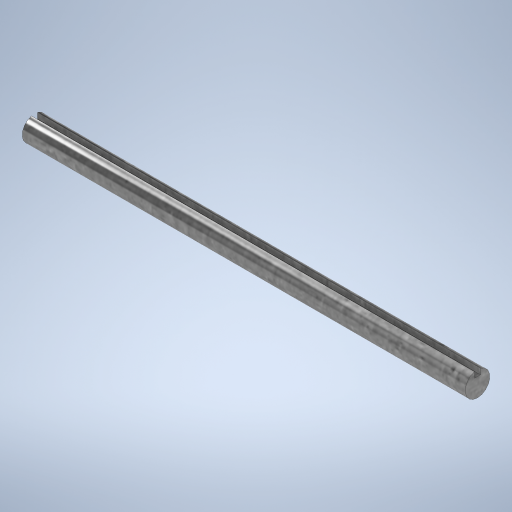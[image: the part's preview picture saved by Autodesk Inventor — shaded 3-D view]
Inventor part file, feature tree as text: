
AUTODESK INVENTOR PART (.ipt)
format: ipt  version: 2023 (Build 270158000, 158)  size: 274,944 bytes
history: native  units: in
note: dims shown in document units (in); Inventor stores cm internally (conversion verified against a paired STEP export)
features: extrude x1, sketch x1
ambient origin geometry x8: Origin, YZ Plane, XZ Plane, XY Plane, X Axis, Y Axis, Z Axis, Center Point
bodies: Solid1 (feature_tree)
feature tree (2):
  extrude  "Extrusion1"  Depth=0.125in
  sketch  "Sketch1"  dims[d0=0.5in d1=0.125in d2=0.25in d3=9.0in d4=0.0in]
